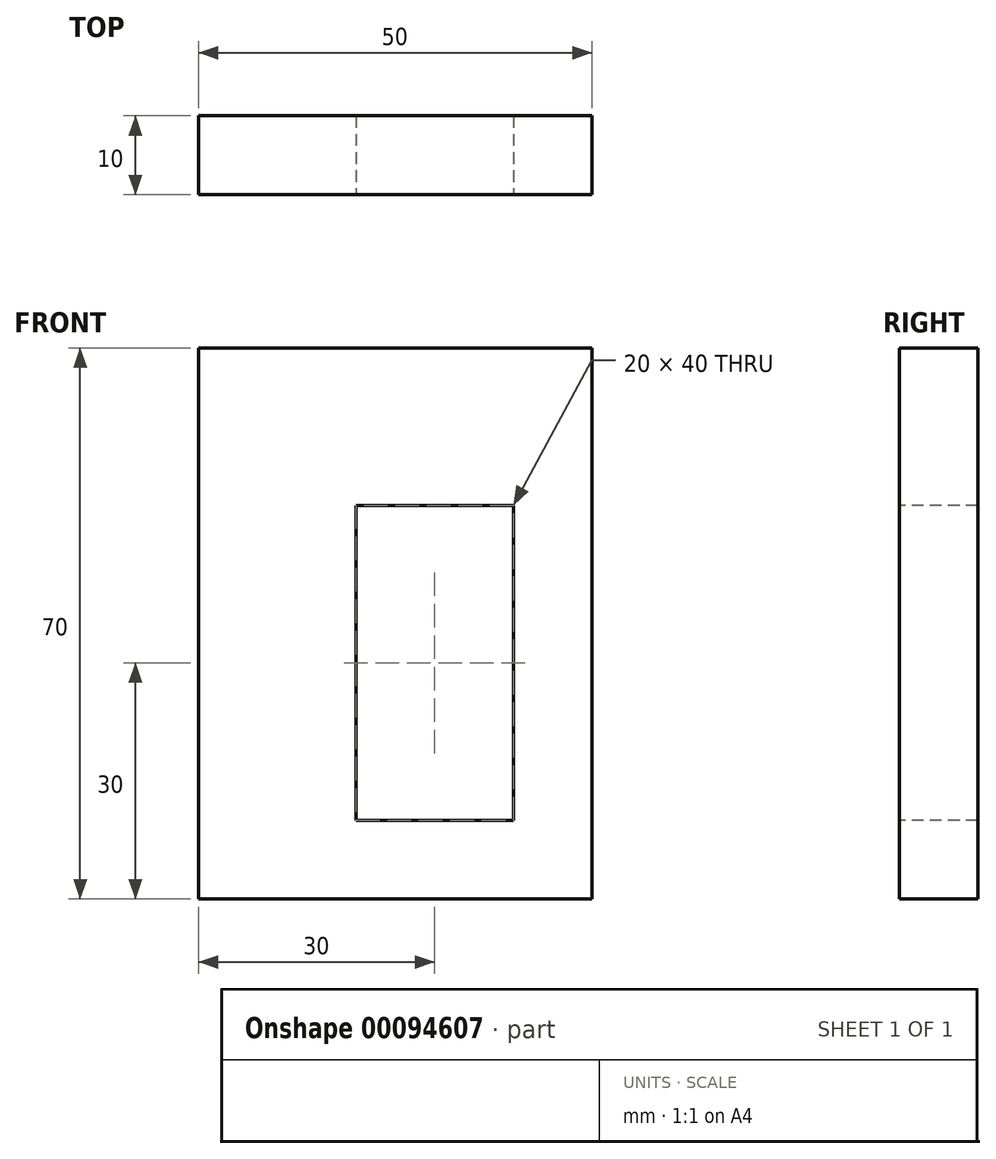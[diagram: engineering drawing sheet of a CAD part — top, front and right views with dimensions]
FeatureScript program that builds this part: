
annotation { "Feature Type Name" : "Feature", "Feature Type Description" : "" }
export const myFeature = defineFeature(function(context is Context, id is Id, definition is map)
    precondition{}
    {
        {
            var Q0;
            Q0=qCreatedBy(makeId("Front.planeOp"),FACE);
            var sketch = newSketch(context, id + "F0", { "sketchPlane" : qUnion([Q0])});
            skLineSegment(sketch, "E0", {"start": v(0, 0) * mm, "end": v(50, 0) * mm});
            skLineSegment(sketch, "E1", {"start": v(50, 0) * mm, "end": v(50, 70) * mm});
            skLineSegment(sketch, "E2", {"start": v(50, 70) * mm, "end": v(0, 70) * mm});
            skLineSegment(sketch, "E3", {"start": v(0, 70) * mm, "end": v(0, 0) * mm});
            skLineSegment(sketch, "E4", {"start": v(20, 50) * mm, "end": v(20, 10) * mm});
            skLineSegment(sketch, "E5", {"start": v(20, 10) * mm, "end": v(40, 10) * mm});
            skLineSegment(sketch, "E6", {"start": v(40, 10) * mm, "end": v(40, 50) * mm});
            skLineSegment(sketch, "E7", {"start": v(40, 50) * mm, "end": v(20, 50) * mm});
            skSolve(sketch);
        }
        {
            var Q0;
            Q0=makeQuery(id+"F0.imprint","IMPRINT",FACE,{"disambiguationData":[TD([[makeQuery(id+"F0.imprint","IMPRINT",EDGE,{"derivedFrom":sQuery(id+"F0.wireOp",EDGE,"E0")}),1.0]])]});
            extrude(context, id + "F1", {"entities" : qUnion([Q0]), "oppositeDirection" : true, "depth" : 10 * mm});
        }
    });
